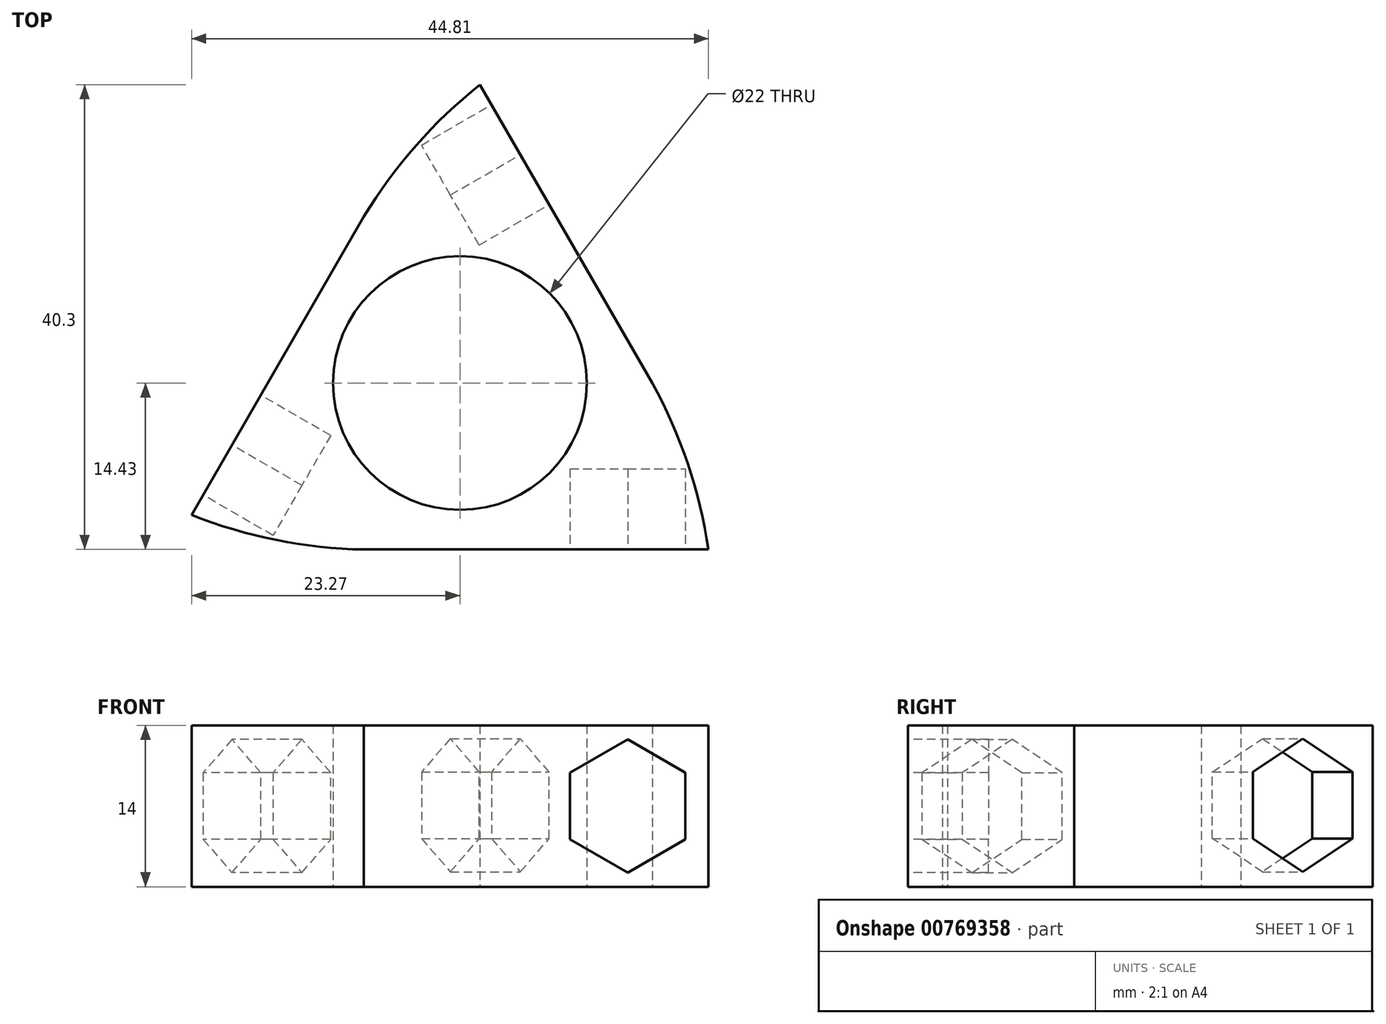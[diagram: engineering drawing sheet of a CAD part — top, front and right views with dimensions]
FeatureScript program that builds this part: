
annotation { "Feature Type Name" : "Feature", "Feature Type Description" : "" }
export const myFeature = defineFeature(function(context is Context, id is Id, definition is map)
    precondition{}
    {
        {
            var Q0;
            Q0=qCreatedBy(makeId("Top.planeOp"),FACE);
            var sketch = newSketch(context, id + "F0", { "sketchPlane" : qUnion([Q0])});
            skCircle(sketch, "E0", {"center": v(0, 0) * mm, "radius": 11 * mm});
            skLineSegment(sketch, "E1", {"start": v(-8.33, 14.43) * mm, "end": v(-25, -14.43) * mm});
            skLineSegment(sketch, "E2", {"start": v(-8.33, -14.43) * mm, "end": v(25, -14.43) * mm});
            skLineSegment(sketch, "E3", {"start": v(16.67, 0) * mm, "end": v(0, 28.87) * mm});
            skLineSegment(sketch, "E4", {"start": v(12.5, 7.22) * mm, "end": v(0, 28.87) * mm});
            skLineSegment(sketch, "E5", {"start": v(0, -14.43) * mm, "end": v(25, -14.43) * mm});
            skLineSegment(sketch, "E6", {"start": v(-12.5, 7.22) * mm, "end": v(-8.33, 14.43) * mm});
            skLineSegment(sketch, "E7", {"start": v(16.67, 0) * mm, "end": v(0, 0) * mm});
            skArc(sketch, "E8", {"start": v(21.54, -14.43) * mm, "mid": v(19.75, -7) * mm, "end": v(16.67, 0) * mm});
            skPoint(sketch, "E9", {"position": v(-23.27, -11.44) * mm});
            skPoint(sketch, "E10", {"position": v(1.73, 25.87) * mm});
            skArc(sketch, "E11", {"start": v(-23.27, -11.44) * mm, "mid": v(-15.94, -13.6) * mm, "end": v(-8.33, -14.43) * mm});
            skArc(sketch, "E12", {"start": v(1.73, 25.87) * mm, "mid": v(-3.81, 20.6) * mm, "end": v(-8.33, 14.43) * mm});
            skSolve(sketch);
        }
        {
            var Q0;
            Q0=makeQuery(id+"F0.imprint","IMPRINT",FACE,{"disambiguationData":[TD([[makeQuery(id+"F0.imprint","IMPRINT",EDGE,{"derivedFrom":sQuery(id+"F0.wireOp",EDGE,"E0")}),-1.0]])]});
            extrude(context, id + "F1", {"entities" : qUnion([Q0]), "depth" : 14 * mm, "offsetDistance" : 25.4 * mm});
        }
        {
            var Q0;
            Q0=makeQuery(id+"F1.opExtrude","SWEPT_FACE",FACE,{"disambiguationData":[OSD([sQuery(id+"F0.wireOp",EDGE,"E3"),sQuery(id+"F0.wireOp",EDGE,"E4")])]});
            var sketch = newSketch(context, id + "F2", { "sketchPlane" : qUnion([Q0])});
            skPoint(sketch, "E13", {"position": v(14.54, 7.07) * mm});
            skCircle(sketch, "E14.cCircle", {"center": v(14.54, 7.07) * mm, "radius": 5 * mm, "construction": true});
            skLineSegment(sketch, "E14.0", {"start": v(19.54, 9.96) * mm, "end": v(19.54, 4.19) * mm});
            skLineSegment(sketch, "E14.1", {"start": v(19.54, 4.19) * mm, "end": v(14.54, 1.3) * mm});
            skLineSegment(sketch, "E14.2", {"start": v(14.54, 1.3) * mm, "end": v(9.54, 4.19) * mm});
            skLineSegment(sketch, "E14.3", {"start": v(9.54, 4.19) * mm, "end": v(9.54, 9.96) * mm});
            skLineSegment(sketch, "E14.4", {"start": v(9.54, 9.96) * mm, "end": v(14.54, 12.85) * mm});
            skLineSegment(sketch, "E14.5", {"start": v(14.54, 12.85) * mm, "end": v(19.54, 9.96) * mm});
            skPoint(sketch, "E14.0.midPoint", {"position": v(19.54, 7.07) * mm});
            skSolve(sketch);
        }
        {
            var Q0;
            Q0=makeQuery(id+"F2.imprint","IMPRINT",FACE,{"disambiguationData":[TD([[makeQuery(id+"F2.imprint","IMPRINT",EDGE,{"derivedFrom":sQuery(id+"F2.wireOp",EDGE,"E14.0")}),-1.0]])]});
            extrude(context, id + "F3", {"entities" : qUnion([Q0]), "operationType" : NewBodyOperationType.REMOVE, "oppositeDirection" : true, "depth" : 7 * mm, "offsetDistance" : 25.4 * mm});
        }
        {
            var Q0;
            Q0=makeQuery(id+"F1.opExtrude","SWEPT_FACE",FACE,{"disambiguationData":[OSD([sQuery(id+"F0.wireOp",EDGE,"E2"),sQuery(id+"F0.wireOp",EDGE,"E5")])]});
            var sketch = newSketch(context, id + "F4", { "sketchPlane" : qUnion([Q0])});
            skPoint(sketch, "E15", {"position": v(14.54, 7) * mm});
            skPoint(sketch, "E15.positionSnap0", {"position": v(21.54, 7) * mm});
            skCircle(sketch, "E16.cCircle", {"center": v(14.54, 7) * mm, "radius": 5 * mm, "construction": true});
            skLineSegment(sketch, "E16.0", {"start": v(19.54, 9.89) * mm, "end": v(19.54, 4.11) * mm});
            skLineSegment(sketch, "E16.1", {"start": v(19.54, 4.11) * mm, "end": v(14.54, 1.23) * mm});
            skLineSegment(sketch, "E16.2", {"start": v(14.54, 1.23) * mm, "end": v(9.54, 4.11) * mm});
            skLineSegment(sketch, "E16.3", {"start": v(9.54, 4.11) * mm, "end": v(9.54, 9.89) * mm});
            skLineSegment(sketch, "E16.4", {"start": v(9.54, 9.89) * mm, "end": v(14.54, 12.77) * mm});
            skLineSegment(sketch, "E16.5", {"start": v(14.54, 12.77) * mm, "end": v(19.54, 9.89) * mm});
            skPoint(sketch, "E16.0.midPoint", {"position": v(19.54, 7) * mm});
            skSolve(sketch);
        }
        {
            var Q0;
            Q0=makeQuery(id+"F4.imprint","IMPRINT",FACE,{"disambiguationData":[TD([[makeQuery(id+"F4.imprint","IMPRINT",EDGE,{"derivedFrom":sQuery(id+"F4.wireOp",EDGE,"E16.0")}),-1.0]])]});
            extrude(context, id + "F5", {"entities" : qUnion([Q0]), "operationType" : NewBodyOperationType.REMOVE, "oppositeDirection" : true, "depth" : 7 * mm, "offsetDistance" : 25.4 * mm});
        }
        {
            var Q0;
            Q0=makeQuery(id+"F1.opExtrude","SWEPT_FACE",FACE,{"disambiguationData":[OSD([sQuery(id+"F0.wireOp",EDGE,"E1"),sQuery(id+"F0.wireOp",EDGE,"E6")])]});
            var sketch = newSketch(context, id + "F6", { "sketchPlane" : qUnion([Q0])});
            skPoint(sketch, "E17", {"position": v(14.54, 7) * mm});
            skCircle(sketch, "E18.cCircle", {"center": v(14.54, 7) * mm, "radius": 5 * mm, "construction": true});
            skLineSegment(sketch, "E18.0", {"start": v(19.54, 9.89) * mm, "end": v(19.54, 4.11) * mm});
            skLineSegment(sketch, "E18.1", {"start": v(19.54, 4.11) * mm, "end": v(14.54, 1.23) * mm});
            skLineSegment(sketch, "E18.2", {"start": v(14.54, 1.23) * mm, "end": v(9.54, 4.11) * mm});
            skLineSegment(sketch, "E18.3", {"start": v(9.54, 4.11) * mm, "end": v(9.54, 9.89) * mm});
            skLineSegment(sketch, "E18.4", {"start": v(9.54, 9.89) * mm, "end": v(14.54, 12.77) * mm});
            skLineSegment(sketch, "E18.5", {"start": v(14.54, 12.77) * mm, "end": v(19.54, 9.89) * mm});
            skPoint(sketch, "E18.0.midPoint", {"position": v(19.54, 7) * mm});
            skSolve(sketch);
        }
        {
            var Q0;
            Q0=makeQuery(id+"F6.imprint","IMPRINT",FACE,{"disambiguationData":[TD([[makeQuery(id+"F6.imprint","IMPRINT",EDGE,{"derivedFrom":sQuery(id+"F6.wireOp",EDGE,"E18.0")}),-1.0]])]});
            extrude(context, id + "F7", {"entities" : qUnion([Q0]), "operationType" : NewBodyOperationType.REMOVE, "oppositeDirection" : true, "depth" : 7 * mm, "offsetDistance" : 25.4 * mm});
        }
    });
